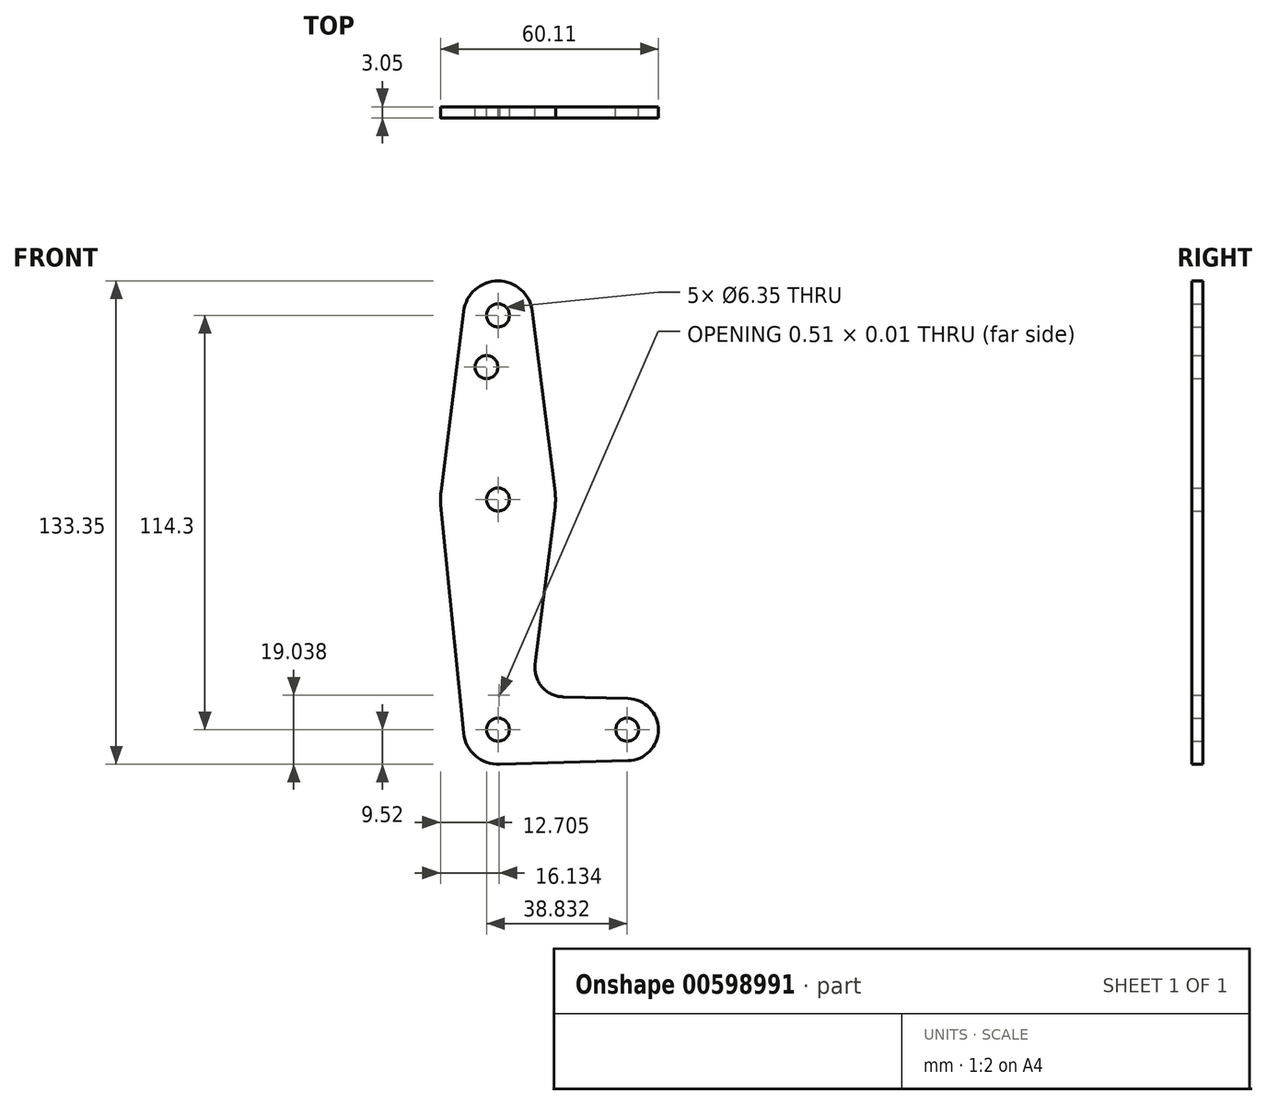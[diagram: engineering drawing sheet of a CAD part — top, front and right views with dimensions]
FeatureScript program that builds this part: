
annotation { "Feature Type Name" : "Feature", "Feature Type Description" : "" }
export const myFeature = defineFeature(function(context is Context, id is Id, definition is map)
    precondition{}
    {
        {
            var Q0;
            Q0=qCreatedBy(makeId("Front.planeOp"),FACE);
            var sketch = newSketch(context, id + "F0", { "sketchPlane" : qUnion([Q0])});
            skLineSegment(sketch, "E0", {"start": v(0, 114.3) * mm, "end": v(0, 0) * mm, "construction": true});
            skCircle(sketch, "E1", {"center": v(0, 114.3) * mm, "radius": 9.53 * mm});
            skCircle(sketch, "E2", {"center": v(0, 63.5) * mm, "radius": 15.88 * mm});
            skCircle(sketch, "E3", {"center": v(0, 0) * mm, "radius": 9.53 * mm});
            skPoint(sketch, "E4.center.orphan", {"position": v(30.76, 0) * mm});
            skPoint(sketch, "E5.orphan", {"position": v(35.66, 0) * mm});
            skLineSegment(sketch, "E6", {"start": v(0, 0) * mm, "end": v(35.66, 0) * mm, "construction": true});
            skCircle(sketch, "E7", {"center": v(35.66, 0) * mm, "radius": 8.57 * mm});
            skLineSegment(sketch, "E8", {"start": v(-9.45, 115.5) * mm, "end": v(-15.75, 65.48) * mm});
            skLineSegment(sketch, "E9", {"start": v(9.45, 115.5) * mm, "end": v(15.75, 65.48) * mm});
            skLineSegment(sketch, "E10", {"start": v(15.75, 61.52) * mm, "end": v(10.27, 17.99) * mm});
            skLineSegment(sketch, "E11", {"start": v(0, 9.53) * mm, "end": v(0.5, 9.51) * mm});
            skLineSegment(sketch, "E12", {"start": v(0, -9.53) * mm, "end": v(35.89, -8.57) * mm});
            skCircle(sketch, "E13", {"center": v(0, 114.3) * mm, "radius": 3.18 * mm});
            skCircle(sketch, "E14", {"center": v(0, 63.5) * mm, "radius": 3.18 * mm});
            skCircle(sketch, "E15", {"center": v(0, 0) * mm, "radius": 3.18 * mm});
            skCircle(sketch, "E16", {"center": v(35.66, 0) * mm, "radius": 3.18 * mm});
            skCircle(sketch, "E17", {"center": v(-3.17, 100.03) * mm, "radius": 3.18 * mm});
            skArc(sketch, "E18", {"start": v(10.27, 17.99) * mm, "mid": v(12.12, 11.82) * mm, "end": v(17.94, 9.05) * mm});
            skLineSegment(sketch, "E19.trimOffspring", {"start": v(17.94, 9.05) * mm, "end": v(35.89, 8.57) * mm});
            skPoint(sketch, "E20.end.orphan", {"position": v(-9.57, 0) * mm});
            skLineSegment(sketch, "E21", {"start": v(-9.48, -0.95) * mm, "end": v(-15.8, 61.91) * mm});
            skSolve(sketch);
        }
        {
            var Q0;
            Q0=qSketchRegion(id+"F0",true);
            extrude(context, id + "F1", {"entities" : qUnion([Q0]), "depth" : 3.05 * mm, "offsetDistance" : 25.4 * mm});
        }
    });
